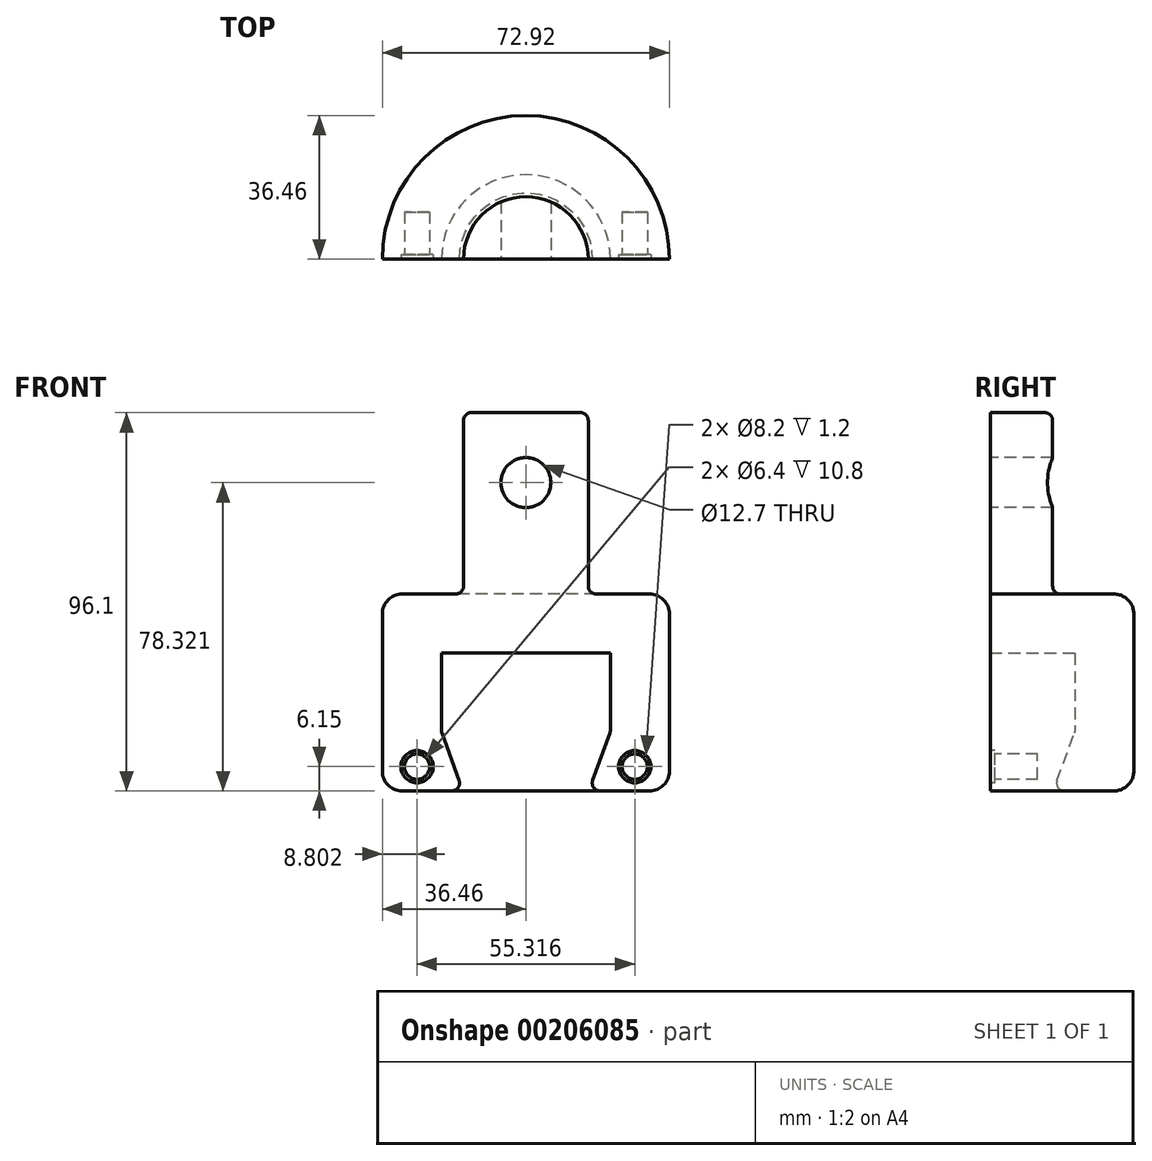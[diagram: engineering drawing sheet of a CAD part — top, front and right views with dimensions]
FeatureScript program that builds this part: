
annotation { "Feature Type Name" : "Feature", "Feature Type Description" : "" }
export const myFeature = defineFeature(function(context is Context, id is Id, definition is map)
    precondition{}
    {
        {
            var Q0;
            Q0=qCreatedBy(makeId("Front.planeOp"),FACE);
            var sketch = newSketch(context, id + "F0", { "sketchPlane" : qUnion([Q0])});
            skLineSegment(sketch, "E0", {"start": v(16, 0) * mm, "end": v(21.46, 15) * mm});
            skLineSegment(sketch, "E1", {"start": v(21.46, 15) * mm, "end": v(21.46, 35) * mm});
            skLineSegment(sketch, "E2", {"start": v(21.46, 35) * mm, "end": v(0, 35) * mm});
            skLineSegment(sketch, "E3", {"start": v(16, 0) * mm, "end": v(36.46, 0) * mm});
            skLineSegment(sketch, "E4", {"start": v(36.46, 0) * mm, "end": v(36.46, 50) * mm});
            skLineSegment(sketch, "E5", {"start": v(36.46, 50) * mm, "end": v(15.85, 50) * mm});
            skLineSegment(sketch, "E6", {"start": v(15.85, 50) * mm, "end": v(15.85, 96.1) * mm});
            skLineSegment(sketch, "E7", {"start": v(15.85, 96.1) * mm, "end": v(0, 96.1) * mm});
            skLineSegment(sketch, "E8", {"start": v(0, 96.1) * mm, "end": v(0, 35) * mm});
            skCircle(sketch, "E9", {"center": v(0, 78.32) * mm, "radius": 6.35 * mm});
            skPoint(sketch, "E10", {"position": v(0, 84.67) * mm});
            skLineSegment(sketch, "E11.bottom", {"start": v(21.46, 35) * mm, "end": v(-21.46, 35) * mm});
            skLineSegment(sketch, "E11.top", {"start": v(21.46, 0) * mm, "end": v(-21.46, 0) * mm});
            skLineSegment(sketch, "E11.left", {"start": v(21.46, 35) * mm, "end": v(21.46, 0) * mm});
            skLineSegment(sketch, "E11.right", {"start": v(-21.46, 35) * mm, "end": v(-21.46, 0) * mm});
            skSolve(sketch);
        }
        {
            var Q0;
            {var subQ0=sQuery(id+"F0.wireOp",EDGE,"E9");var subQ1=sQuery(id+"F0.wireOp",EDGE,"E8");var subQ2=makeQuery(id+"F0.imprint","INTERSECT",VERTEX,{"disambiguationData":[OD(0.0)],"derivedFrom":[subQ1,subQ0]});Q0=makeQuery(id+"F0.imprint","IMPRINT",FACE,{"disambiguationData":[TD([[makeQuery(id+"F0.imprint","IMPRINT",EDGE,{"disambiguationData":[TD([[subQ2,-1.0]])],"derivedFrom":subQ1}),1.0]])]});}
            var Q1;
            {var subQ10=sQuery(id+"F0.wireOp",EDGE,"E3");Q1=makeQuery(id+"F0.imprint","IMPRINT",FACE,{"disambiguationData":[TD([[makeQuery(id+"F0.imprint","IMPRINT",EDGE,{"derivedFrom":subQ10}),1.0]])]});}
            var Q2;
            {var subQ0=sQuery(id+"F0.wireOp",EDGE,"E0");Q2=makeQuery(id+"F0.imprint","IMPRINT",FACE,{"disambiguationData":[TD([[makeQuery(id+"F0.imprint","IMPRINT",EDGE,{"derivedFrom":subQ0}),-1.0]])]});}
            var Q3;
            Q3=sQuery(id+"F0.wireOp",EDGE,"E8");
            revolve(context, id + "F1", {"entities" : qUnion([Q0, Q1, Q2]), "axis" : qUnion([Q3]), "revolveType" : RevolveType.ONE_DIRECTION, "oppositeDirection" : true, "angle" : 180 * degree});
        }
        {
            var Q0;
            Q0=makeQuery(id+"F1.opRevolve","SWEPT_EDGE",EDGE,{"disambiguationData":[OSD([sQuery(id+"F0.wireOp",EDGE,"E5"),sQuery(id+"F0.wireOp",EDGE,"E6")])]});
            var Q1;
            Q1=makeQuery(id+"F1.opRevolve","SWEPT_EDGE",EDGE,{"disambiguationData":[OSD([sQuery(id+"F0.wireOp",EDGE,"E6"),sQuery(id+"F0.wireOp",EDGE,"E7")])]});
            var Q2;
            Q2=makeQuery(id+"F1.opRevolve","SWEPT_EDGE",EDGE,{"disambiguationData":[OSD([sQuery(id+"F0.wireOp",EDGE,"E0"),sQuery(id+"F0.wireOp",EDGE,"E11.top")])]});
            var Q3;
            Q3=makeQuery(id+"F1.opRevolve","SWEPT_EDGE",EDGE,{"disambiguationData":[OSD([sQuery(id+"F0.wireOp",EDGE,"E0"),sQuery(id+"F0.wireOp",EDGE,"E11.left")])]});
            fillet(context, id + "F2", {"entities" : qUnion([Q0, Q1, Q2, Q3]), "radius" : 2 * mm, "tangentPropagation" : true, "allowEdgeOverflow" : false});
        }
        {
            var Q0;
            Q0=qCreatedBy(makeId("Front.planeOp"),FACE);
            var sketch = newSketch(context, id + "F3", { "sketchPlane" : qUnion([Q0])});
            skCircle(sketch, "E12", {"center": v(0, 78.32) * mm, "radius": 6.35 * mm});
            skCircle(sketch, "E13", {"center": v(27.66, 6.15) * mm, "radius": 4.1 * mm});
            skCircle(sketch, "E14", {"center": v(-27.66, 6.15) * mm, "radius": 4.1 * mm});
            skLineSegment(sketch, "E15", {"start": v(27.66, 2.05) * mm, "end": v(27.66, 0) * mm, "construction": true});
            skLineSegment(sketch, "E16", {"start": v(27.66, 4.1) * mm, "end": v(27.66, 6.15) * mm, "construction": true});
            skLineSegment(sketch, "E17", {"start": v(27.66, 4.1) * mm, "end": v(27.66, 2.05) * mm, "construction": true});
            skCircle(sketch, "E18", {"center": v(27.66, 6.15) * mm, "radius": 3.2 * mm});
            skCircle(sketch, "E19", {"center": v(-27.66, 6.15) * mm, "radius": 3.2 * mm});
            skLineSegment(sketch, "E20", {"start": v(-27.66, 6.15) * mm, "end": v(27.66, 6.15) * mm, "construction": true});
            skPoint(sketch, "E21", {"position": v(0, 6.15) * mm});
            skSolve(sketch);
        }
        {
            var Q0;
            Q0=makeQuery(id+"F3.imprint","IMPRINT",FACE,{"disambiguationData":[TD([[makeQuery(id+"F3.imprint","IMPRINT",EDGE,{"derivedFrom":sQuery(id+"F3.wireOp",EDGE,"E13")}),1.0]])]});
            var Q1;
            Q1=makeQuery(id+"F3.imprint","IMPRINT",FACE,{"disambiguationData":[TD([[makeQuery(id+"F3.imprint","IMPRINT",EDGE,{"derivedFrom":sQuery(id+"F3.wireOp",EDGE,"E14")}),1.0]])]});
            var Q2;
            Q2=makeQuery(id+"F3.imprint","IMPRINT",FACE,{"disambiguationData":[TD([[makeQuery(id+"F3.imprint","IMPRINT",EDGE,{"derivedFrom":sQuery(id+"F3.wireOp",EDGE,"E19")}),1.0]])]});
            var Q3;
            Q3=makeQuery(id+"F3.imprint","IMPRINT",FACE,{"disambiguationData":[TD([[makeQuery(id+"F3.imprint","IMPRINT",EDGE,{"derivedFrom":sQuery(id+"F3.wireOp",EDGE,"E18")}),1.0]])]});
            extrude(context, id + "F4", {"entities" : qUnion([Q0, Q1, Q2, Q3]), "operationType" : NewBodyOperationType.REMOVE, "oppositeDirection" : true, "depth" : 1.2 * mm});
        }
        {
            var Q0;
            Q0=makeQuery(id+"F3.imprint","IMPRINT",FACE,{"disambiguationData":[TD([[makeQuery(id+"F3.imprint","IMPRINT",EDGE,{"derivedFrom":sQuery(id+"F3.wireOp",EDGE,"E19")}),1.0]])]});
            var Q1;
            Q1=makeQuery(id+"F3.imprint","IMPRINT",FACE,{"disambiguationData":[TD([[makeQuery(id+"F3.imprint","IMPRINT",EDGE,{"derivedFrom":sQuery(id+"F3.wireOp",EDGE,"E18")}),1.0]])]});
            extrude(context, id + "F5", {"entities" : qUnion([Q0, Q1]), "operationType" : NewBodyOperationType.REMOVE, "oppositeDirection" : true, "depth" : 12 * mm});
        }
        {
            var Q0;
            Q0=makeQuery(id+"F3.imprint","IMPRINT",FACE,{"disambiguationData":[TD([[makeQuery(id+"F3.imprint","IMPRINT",EDGE,{"derivedFrom":sQuery(id+"F3.wireOp",EDGE,"E12")}),1.0]])]});
            extrude(context, id + "F6", {"entities" : qUnion([Q0]), "operationType" : NewBodyOperationType.REMOVE, "endBound" : BoundingType.THROUGH_ALL, "oppositeDirection" : true, "depth" : 25 * mm});
        }
        {
            var Q0;
            Q0=makeQuery(id+"F1.opRevolve","SWEPT_EDGE",EDGE,{"disambiguationData":[OSD([sQuery(id+"F0.wireOp",EDGE,"E4"),sQuery(id+"F0.wireOp",EDGE,"E5")])]});
            var Q1;
            Q1=makeQuery(id+"F1.opRevolve","SWEPT_EDGE",EDGE,{"disambiguationData":[OSD([sQuery(id+"F0.wireOp",EDGE,"E3"),sQuery(id+"F0.wireOp",EDGE,"E4")])]});
            var Q2;
            Q2=makeQuery(id+"F1.opRevolve","SWEPT_EDGE",EDGE,{"disambiguationData":[OSD([sQuery(id+"F0.wireOp",EDGE,"E11.bottom"),sQuery(id+"F0.wireOp",EDGE,"E11.left")])]});
            fillet(context, id + "F7", {"entities" : qUnion([Q0, Q1, Q2]), "radius" : 5 * mm, "tangentPropagation" : true, "allowEdgeOverflow" : false});
        }
    });
